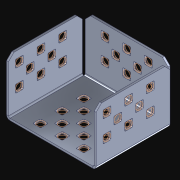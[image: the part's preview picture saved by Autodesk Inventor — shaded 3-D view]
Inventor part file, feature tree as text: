
AUTODESK INVENTOR PART (.ipt)
format: ipt  version: 2021.3 (Build 253353010, 353A)  size: 758,784 bytes
history: native  units: in
note: dims shown in document units (in); Inventor stores cm internally (conversion verified against a paired STEP export)
features: other x38, extrude x37, pattern_linear x8, imported_body x1, sketch x1
ambient origin geometry x8: Origin, YZ Plane, XZ Plane, XY Plane, X Axis, Y Axis, Z Axis, Center Point
bodies: Body1 (feature_tree), Body2 (feature_tree), Body3 (feature_tree), Body4 (feature_tree), Body5 (feature_tree), Body6 (feature_tree), Body7 (feature_tree), Body8 (feature_tree), Body9 (feature_tree), Body10 (feature_tree), Body11 (feature_tree), Body12 (feature_tree), Body13 (feature_tree), Body14 (feature_tree), Body15 (feature_tree), Body16 (feature_tree), Body17 (feature_tree), Body18 (feature_tree), Body19 (feature_tree), Body20 (feature_tree), Body21 (feature_tree), Body22 (feature_tree), Body23 (feature_tree), Body24 (feature_tree), Body25 (feature_tree), Body26 (feature_tree), Body27 (feature_tree), Body28 (feature_tree), Body29 (feature_tree), Body30 (feature_tree), Body31 (feature_tree), Body32 (feature_tree), Body33 (feature_tree), Body34 (feature_tree), Body35 (feature_tree), Body36 (feature_tree), Body37 (feature_tree), Body38 (feature_tree)
feature tree (85):
  parser-record x1  (decoder bookkeeping rows leaked as tree rows — omitted from the tree; the rows remain in map.json)
  imported_body  "Base1"
  pattern_linear  "Rectangular Pattern1"  Count1=3 Spacing1=0.5in
  pattern_linear  "Rectangular Pattern2"  Count1=2 Spacing1=0.5in
  pattern_linear  "Rectangular Pattern3"  Spacing1=0.046in  [1 undecoded]
  pattern_linear  "Rectangular Pattern4"  Count1=2 Spacing1=0.5in
  pattern_linear  "Rectangular Pattern5"  Spacing1=0.046in  [1 undecoded]
  pattern_linear  "Rectangular Pattern6"  Count1=3 Spacing1=0.5in
  pattern_linear  "Rectangular Pattern7"  Count1=2 Spacing1=0.5in
  pattern_linear  "Rectangular Pattern8"  Spacing1=0.046in  [1 undecoded]
  other  "Srf1"
  other  "Srf2"
  other  "Srf3"
  other  "Srf4"
  other  "Srf5"
  other  "Srf6"
  other  "Srf7"
  other  "Srf8"
  other  "Srf9"
  other  "Srf10"
  other  "Srf11"
  other  "Srf12"
  other  "Srf13"
  other  "Srf14"
  other  "Srf15"
  other  "Srf16"
  other  "Srf17"
  other  "Srf18"
  other  "Srf19"
  other  "Srf20"
  other  "Srf21"
  other  "Srf22"
  other  "Srf23"
  other  "Srf24"
  other  "Srf25"
  other  "Srf26"
  other  "Srf27"
  other  "Srf28"
  other  "Srf29"
  other  "Srf30"
  other  "Srf31"
  other  "Srf32"
  other  "Srf33"
  sketch  "Sketch8"  dims[d118=0.046in d119=0.0in d120=1.1811in d122=0.5in d123=0.7874in d125=0.5in d127=0.046in d128=0.0in d129=0.7874in d131=0.5in d133=0.046in d134=0.0in d135=1.1811in d137=0.5in d138=0.7874in d140=0.5in d142=0.046in d143=0.0in d144=0.7874in d146=0.5in d148=0.046in d149=0.0in d150=1.1811in d152=0.5in d153=0.7874in d155=0.5in d157=0.046in d158=0.0in d159=0.7874in d161=0.5in d163=0.046in d164=0.0in d165=1.1811in d167=0.5in d168=1.1811in d170=0.5in d171=0.167in d172=0.046in d173=0.0in d174=0.7874in d176=0.5in d177=0.7874in d179=0.5in]
  other  "Srf34"
  other  "Srf35"
  other  "Srf36"
  other  "Srf37"
  extrude  "ExtrusionSrf1"  Depth=0.5in
  extrude  "ExtrusionSrf7"  Depth=0.046in TaperAngle=0.0deg
  extrude  "ExtrusionSrf9"  Depth=0.5in
  extrude  "ExtrusionSrf15"  Depth=0.5in
  extrude  "ExtrusionSrf17"  Depth=0.046in TaperAngle=0.0deg
  extrude  "ExtrusionSrf23"  Depth=0.5in
  extrude  "ExtrusionSrf25"  Depth=0.046in TaperAngle=0.0deg
  extrude  "ExtrusionSrf34"  Depth=0.5in
  extrude  "ExtrusionSrf2"  Depth=0.5in
  extrude  "ExtrusionSrf3"  Depth=0.5in
  extrude  "ExtrusionSrf4"  Depth=0.046in TaperAngle=0.0deg
  extrude  "ExtrusionSrf5"  Depth=0.5in
  extrude  "ExtrusionSrf6"  Depth=0.5in
  extrude  "ExtrusionSrf8"  [1 undecoded]
  extrude  "ExtrusionSrf10"  [1 undecoded]
  extrude  "ExtrusionSrf11"  [1 undecoded]
  extrude  "ExtrusionSrf12"  [1 undecoded]
  extrude  "ExtrusionSrf13"  [1 undecoded]
  extrude  "ExtrusionSrf14"  [1 undecoded]
  extrude  "ExtrusionSrf16"  [1 undecoded]
  extrude  "ExtrusionSrf18"  [1 undecoded]
  extrude  "ExtrusionSrf19"  [1 undecoded]
  extrude  "ExtrusionSrf20"  [1 undecoded]
  extrude  "ExtrusionSrf21"  [1 undecoded]
  extrude  "ExtrusionSrf22"  [1 undecoded]
  extrude  "ExtrusionSrf24"  [1 undecoded]
  extrude  "ExtrusionSrf26"  [1 undecoded]
  extrude  "ExtrusionSrf27"  [1 undecoded]
  extrude  "ExtrusionSrf28"  [1 undecoded]
  extrude  "ExtrusionSrf29"  [1 undecoded]
  extrude  "ExtrusionSrf30"  [1 undecoded]
  extrude  "ExtrusionSrf31"  [1 undecoded]
  extrude  "ExtrusionSrf32"  [1 undecoded]
  extrude  "ExtrusionSrf33"  [1 undecoded]
  extrude  "ExtrusionSrf35"  [1 undecoded]
  extrude  "ExtrusionSrf36"  [1 undecoded]
  extrude  "ExtrusionSrf37"  [1 undecoded]
note: 27 required parameter values undecoded (feature->parameter linkage not recoverable at this tier; creation-order binding heuristic only, values carry confidence <= 0.55)
